# Revit family: Thorn BETA3
name_source: partatom
category: Leuchten
revit_build: Autodesk Revit 2016 (Build: 20150220_1215(x64)
units: mm (PartAtom-declared; Revit-internal decimal feet)

## family parameters
Basisbauteil = Fläche
Beim Laden mit Abzugskörper schneiden = Nein
Bemaßung runder Anschluss = Durchmesser verwenden
Gemeinsam genutzt = Nein
Lichtquelle = Ja
OmniClass-Nummer = 23.80.70.11
OmniClass-Titel = Luminaries for Internal Lighting
Raumberechnungspunkt = Nein
Teiletyp = Normal

## types (3) — shared parameters
Baugruppenkennzeichen = D5020200
Beschreibung = Recessed LED luminaire
Body = Thorn_Metal_White
Cover = Thorn_PMMA_Opaque
Emissionsform beim Rendern sichtbar = Nein
Farbfilter = 16777215
Farbtemperaturverschiebung bei Dämpfen der Lampe = <Keine Auswahl>
Height = 34 mm
Hersteller = Thorn Lighting
Lampe = LED
Neigungswinkel = -90.00°
Scheinlast = 34 VA
Voltage = 230 V
zero-valued in all types: Vorgabe-Ansicht

## per-type parameters (varying)
| type | Datei für fotometrisches Netz | Length | Modell | URL | Von Breite des Rechtecks ausssenden | Von Länge des Rechtecks aussenden | Width |
| BETA 3 Q600 4100-840 HFIX | 96634494_(STD).IES | 596 mm | 96634494 | www.thornlighting.com/96634494 | 546 mm | 546 mm | 596 mm |
| BETA 3 Q625 4100-840 HFIX | 96634494_(STD).IES | 622 mm  [stored 2.04068 ft] | 96634505 | www.thornlighting.com/96634505 | 572 mm | 572 mm | 622 mm  [stored 2.04068 ft] |
| BETA 3 3X12 4100-840 HFIX | 96634512_(STD).IES | 1196 mm | 96634512 | www.thornlighting.com/96634512 | 1146 mm | 246 mm | 296 mm |

note: [stored X ft] marks values corroborated as IEEE doubles in the binary element streams (Revit-internal decimal feet)

## geometry (parser evidence)
native form markers: Sweep x3
no freeform markers — native parametric forms only
